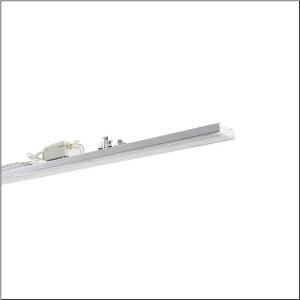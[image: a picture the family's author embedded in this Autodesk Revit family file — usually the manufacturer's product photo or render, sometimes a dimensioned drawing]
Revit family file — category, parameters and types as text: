
# Revit family: licross_r__21_recessed_ho_52te11dv4l2s_a4a6
name_source: partatom
category: Lighting Fixtures
units: mm (PartAtom-declared; Revit-internal decimal feet)

## family parameters
Cut with Voids When Loaded = No
Host = Face
Light Source = No
Part Type = Normal
Room Calculation Point = No
Round Connector Dimension = Use Diameter
Shared = No

## types (1)
- --- (1 x LED, 22660 lm, 125.6 W, 4000K)
    Apparent Load = 126 VA
    CIE Flux Codes = 87 95 99 100 100
    Color Rendering = 80
    Color Temperature = 4000K
    Default Elevation = 1800 mm
    Description = Licross® 21 Recessed HO, luminaire insert, of sheet steel, galvanised, coil coated, white, length: 2.250mm, width: 66mm, height: 67mm, LED rated luminous flux: 22.660lm, light colour: 840, control gear: DALI 2, with plug, 5-pole, with phase selection, mains connection: 220..240V, AC, 50/60Hz, rated input power: 126W, halogen-free wiring, primary light control with lens, of plastic, primary optical cover: cover, of PMMA, light emission: direct distribution, primary light characteristic: symmetric, protection rating (complete): IP54, insulation class (complete): insulation class I (protective earthing), certification: CE, ENEC, VDE, UKCA, protection symbol: D if used in an environment with non-conductive dust loads with corresponding accessories, impact resistance: IK06, permissible ambient temperature for indoor applications: -40..+30°C, corresponds to IFS (International Featured Standards) requirements for safety and quality in the food industry, reducing of maximum allowable ambient temperature of 5°C with ceiling mounting, LABS conformity tested according to VDMA 24364:2018-05, packaging unit: 1 piece
    Height = 58 mm
    Lamp = 1 x LED
    Lamp Light Flux = 22660 lm
    Lamp Power = 125.6 W
    Lamp count = 1
    Length = 2250 mm
    Luminous efficacy = 180 lm/W
    Manufacturer = Siteco
    ModVariant = No
    Model = 52TE11DV4L2S
    Mounting Place = Ceiling
    Mounting Type = Pendant
    Number of Poles = 1
    OnlyDefault = Yes
    Power Factor = 1
    Product Name = Licross® 21 Recessed HO
    Product group = luminaire insert
    ProductGroupID = 901
    Protection Class = Protection class I
    Protection Degree = IP 54
    RLX_Detail_Level = 1
    RLX_Emergency_Light_Flux = 0 lm
    RLX_Emergency_Type = 0
    RLX_Emergency_Type_DB = No
    RlxData = <blob elided: 29661 chars, md5=98111165>
    Socket = socket
    Standby Power = 0 W
    System Light Flux = 22659 lm
    System Power = 126 W
    Type Comments = factory setting: luminous flux: 100 % | dim-lin: 254 | 489 mA
    Type Image = l_1296930.jpg
    URL = http://relux.com
    VarID = @adj_058989
    Voltage = 0 V
    Weight = 0.00 kg
    Width = 66 mm

## geometry (parser evidence)
native form markers: Blend x4, Sweep x10
no freeform markers — native parametric forms only
